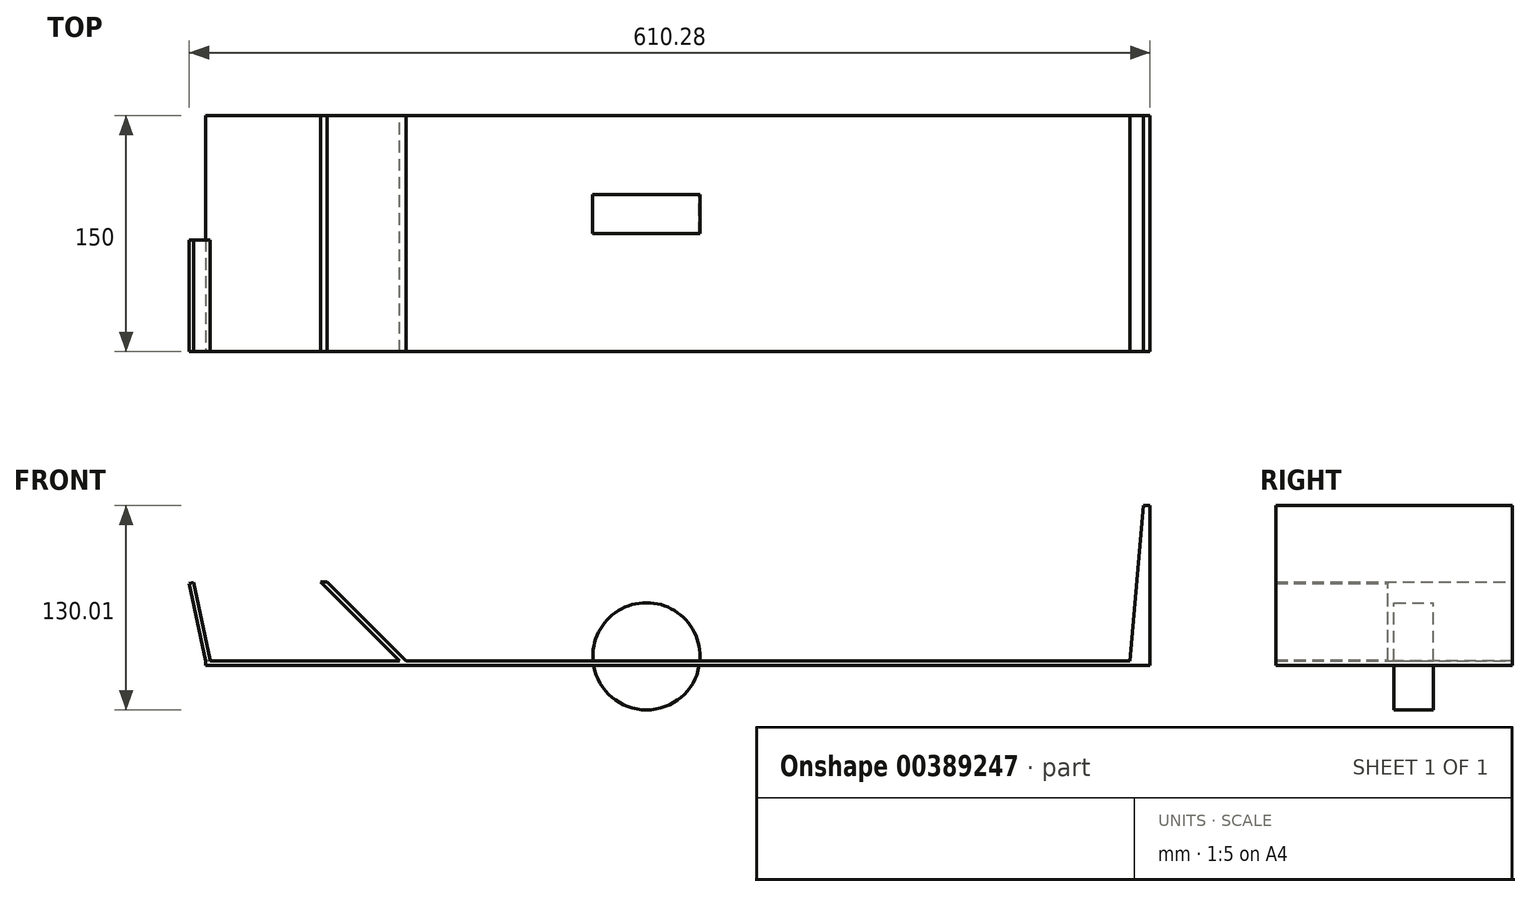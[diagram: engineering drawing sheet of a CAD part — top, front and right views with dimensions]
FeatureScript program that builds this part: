
annotation { "Feature Type Name" : "Feature", "Feature Type Description" : "" }
export const myFeature = defineFeature(function(context is Context, id is Id, definition is map)
    precondition{}
    {
        {
            var Q0;
            Q0=qCreatedBy(makeId("Top.planeOp"),FACE);
            var sketch = newSketch(context, id + "F0", { "sketchPlane" : qUnion([Q0])});
            skLineSegment(sketch, "E0.bottom", {"start": v(-298.36, 0) * mm, "end": v(301.64, 0) * mm});
            skLineSegment(sketch, "E0.top", {"start": v(-298.36, -150) * mm, "end": v(301.64, -150) * mm});
            skLineSegment(sketch, "E0.left", {"start": v(-298.36, 0) * mm, "end": v(-298.36, -150) * mm});
            skLineSegment(sketch, "E0.right", {"start": v(301.64, 0) * mm, "end": v(301.64, -150) * mm});
            skSolve(sketch);
        }
        {
            var Q0;
            Q0 = qSketchRegion(id + "F0", true);
            extrude(context, id + "F1", {"entities" : qUnion([Q0]), "depth" : 3 * mm, "offsetDistance" : 25 * mm});
        }
        {
            var Q0;
            Q0=qCreatedBy(makeId("Front.planeOp"),FACE);
            var sketch = newSketch(context, id + "F2", { "sketchPlane" : qUnion([Q0])});
            skLineSegment(sketch, "E1", {"start": v(-298.36, 3) * mm, "end": v(-308.64, 51.93) * mm});
            skLineSegment(sketch, "E2.0", {"start": v(-295.42, 3.62) * mm, "end": v(-305.7, 52.55) * mm});
            skLineSegment(sketch, "E3", {"start": v(-305.7, 52.55) * mm, "end": v(-308.64, 51.93) * mm});
            skLineSegment(sketch, "E4", {"start": v(-295.42, 3.62) * mm, "end": v(-295.42, 2.94) * mm});
            skLineSegment(sketch, "E5", {"start": v(-295.42, 2.94) * mm, "end": v(-298.36, 3) * mm});
            skSolve(sketch);
        }
        {
            var Q0;
            Q0=makeQuery(id+"F2.imprint","IMPRINT",FACE,{"disambiguationData":[TD([[makeQuery(id+"F2.imprint","IMPRINT",EDGE,{"derivedFrom":sQuery(id+"F2.wireOp",EDGE,"E1")}),-1.0]])]});
            extrude(context, id + "F3", {"entities" : qUnion([Q0]), "operationType" : NewBodyOperationType.ADD, "depth" : 150 * mm, "offsetDistance" : 25 * mm});
        }
        {
            var Q0;
            Q0=makeQuery(id+"F3.boolean.opBoolean","MERGE",FACE,{"derivedFrom":[makeQuery(id+"F1.opExtrude","SWEPT_FACE",FACE,{"disambiguationData":[OSD([sQuery(id+"F0.wireOp",EDGE,"E0.bottom")])]}),makeQuery(id+"F3.opExtrude","CAP_FACE",FACE,{"disambiguationData":[OSD([sQuery(id+"F2.wireOp",EDGE,"E1"),sQuery(id+"F2.wireOp",EDGE,"E2.0"),sQuery(id+"F2.wireOp",EDGE,"E3"),sQuery(id+"F2.wireOp",EDGE,"E4"),sQuery(id+"F2.wireOp",EDGE,"E5")])],"isStart":true})]});
            var sketch = newSketch(context, id + "F4", { "sketchPlane" : qUnion([Q0])});
            skLineSegment(sketch, "E6", {"start": v(295.42, 3) * mm, "end": v(298.36, 3) * mm});
            skSolve(sketch);
        }
        {
            var Q0;
            Q0=makeQuery(id+"F4.imprint","IMPRINT",FACE,{"disambiguationData":[TD([[makeQuery(id+"F4.imprint","IMPRINT",EDGE,{"derivedFrom":sQuery(id+"F4.wireOp",EDGE,"E6")}),1.0]])]});
            extrude(context, id + "F5", {"entities" : qUnion([Q0]), "operationType" : NewBodyOperationType.REMOVE, "oppositeDirection" : true, "depth" : 79 * mm, "offsetDistance" : 25 * mm});
        }
        {
            var Q0;
            Q0=qCreatedBy(makeId("Front.planeOp"),FACE);
            cPlane(context, id + "F6", {"entities" : qUnion([Q0]), "cplaneType" : CPlaneType.OFFSET, "offset" : 50 * mm, "width" : 150 * mm, "height" : 150 * mm});
        }
        {
            var Q0;
            Q0=qCreatedBy(id+"F6.planeOp",FACE);
            var sketch = newSketch(context, id + "F7", { "sketchPlane" : qUnion([Q0])});
            skCircle(sketch, "E7", {"center": v(-18.26, 5.77) * mm, "radius": 34.05 * mm});
            skSolve(sketch);
        }
        {
            var Q0;
            Q0 = qSketchRegion(id + "F7", true);
            extrude(context, id + "F8", {"entities" : qUnion([Q0]), "operationType" : NewBodyOperationType.ADD, "depth" : 25 * mm, "offsetDistance" : 25 * mm});
        }
        {
            var Q0;
            Q0=qCreatedBy(makeId("Front.planeOp"),FACE);
            var sketch = newSketch(context, id + "F9", { "sketchPlane" : qUnion([Q0])});
            skLineSegment(sketch, "E8.bottom", {"start": v(301.64, 3) * mm, "end": v(232.99, 3) * mm});
            skLineSegment(sketch, "E8.top", {"start": v(301.64, 101.73) * mm, "end": v(232.99, 101.73) * mm});
            skLineSegment(sketch, "E8.left", {"start": v(301.64, 3) * mm, "end": v(301.64, 101.73) * mm});
            skLineSegment(sketch, "E8.right", {"start": v(232.99, 3) * mm, "end": v(232.99, 101.73) * mm});
            skSolve(sketch);
        }
        {
            var Q0;
            Q0 = qSketchRegion(id + "F9", true);
            extrude(context, id + "F10", {"entities" : qUnion([Q0]), "operationType" : NewBodyOperationType.ADD, "depth" : 150 * mm, "offsetDistance" : 25 * mm});
        }
        {
            var Q0;
            Q0=makeQuery(id+"F10.boolean.opBoolean","MERGE",FACE,{"derivedFrom":[makeQuery(id+"F3.boolean.opBoolean","MERGE",FACE,{"derivedFrom":[makeQuery(id+"F1.opExtrude","SWEPT_FACE",FACE,{"disambiguationData":[OSD([sQuery(id+"F0.wireOp",EDGE,"E0.top")])]}),makeQuery(id+"F3.opExtrude","CAP_FACE",FACE,{"disambiguationData":[OSD([sQuery(id+"F2.wireOp",EDGE,"E1"),sQuery(id+"F2.wireOp",EDGE,"E2.0"),sQuery(id+"F2.wireOp",EDGE,"E3"),sQuery(id+"F2.wireOp",EDGE,"E4"),sQuery(id+"F2.wireOp",EDGE,"E5")])],"isStart":false})]}),makeQuery(id+"F10.opExtrude","CAP_FACE",FACE,{"disambiguationData":[OSD([sQuery(id+"F9.wireOp",EDGE,"E8.bottom"),sQuery(id+"F9.wireOp",EDGE,"E8.top"),sQuery(id+"F9.wireOp",EDGE,"E8.left"),sQuery(id+"F9.wireOp",EDGE,"E8.right")])],"isStart":false})]});
            var sketch = newSketch(context, id + "F11", { "sketchPlane" : qUnion([Q0])});
            skLineSegment(sketch, "E9", {"start": v(232.99, 3) * mm, "end": v(288.84, 3) * mm});
            skLineSegment(sketch, "E10", {"start": v(288.84, 3) * mm, "end": v(297.43, 101.73) * mm});
            skLineSegment(sketch, "E11", {"start": v(297.43, 101.73) * mm, "end": v(232.99, 101.73) * mm});
            skLineSegment(sketch, "E12", {"start": v(232.99, 101.73) * mm, "end": v(232.99, 3) * mm});
            skSolve(sketch);
        }
        {
            var Q0;
            Q0 = qSketchRegion(id + "F11", true);
            extrude(context, id + "F12", {"entities" : qUnion([Q0]), "operationType" : NewBodyOperationType.REMOVE, "endBound" : BoundingType.THROUGH_ALL, "oppositeDirection" : true, "depth" : 25 * mm, "offsetDistance" : 25 * mm});
        }
        {
            var Q0;
            Q0=qCreatedBy(makeId("Front.planeOp"),FACE);
            var sketch = newSketch(context, id + "F13", { "sketchPlane" : qUnion([Q0])});
            skLineSegment(sketch, "E13", {"start": v(-175.08, 3) * mm, "end": v(-225.08, 53) * mm});
            skLineSegment(sketch, "E14.0", {"start": v(-187.8, 19.96) * mm, "end": v(-220.97, 53.13) * mm});
            skLineSegment(sketch, "E15", {"start": v(-220.97, 53.13) * mm, "end": v(-225.08, 53) * mm});
            skLineSegment(sketch, "E16", {"start": v(-187.8, 19.96) * mm, "end": v(-170.83, 3) * mm});
            skLineSegment(sketch, "E17", {"start": v(-170.83, 3) * mm, "end": v(-175.08, 3) * mm});
            skSolve(sketch);
        }
        {
            var Q0;
            Q0 = qSketchRegion(id + "F13", true);
            extrude(context, id + "F14", {"entities" : qUnion([Q0]), "operationType" : NewBodyOperationType.ADD, "depth" : 150 * mm, "offsetDistance" : 25 * mm});
        }
    });
